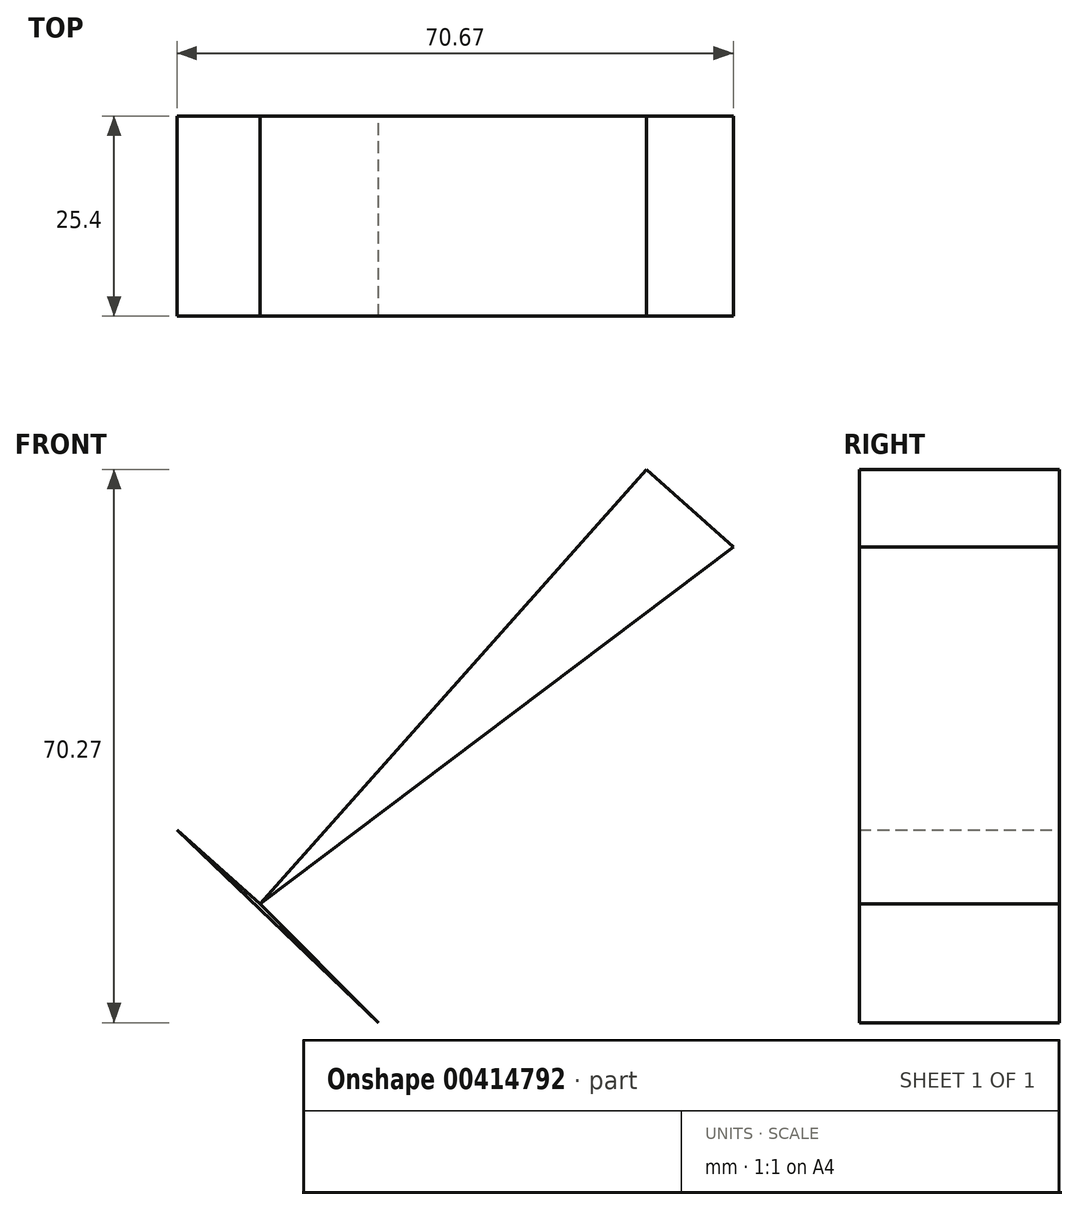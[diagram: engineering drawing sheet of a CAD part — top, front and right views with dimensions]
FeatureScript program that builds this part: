
annotation { "Feature Type Name" : "Feature", "Feature Type Description" : "" }
export const myFeature = defineFeature(function(context is Context, id is Id, definition is map)
    precondition{}
    {
        {
            var Q0;
            Q0=qCreatedBy(makeId("Front.planeOp"),FACE);
            var sketch = newSketch(context, id + "F0", { "sketchPlane" : qUnion([Q0])});
            skLineSegment(sketch, "E0", {"start": v(0, 9.82) * mm, "end": v(0, 0) * mm});
            skLineSegment(sketch, "E1", {"start": v(0, 0) * mm, "end": v(11.04, 0) * mm});
            skLineSegment(sketch, "E2", {"start": v(11.04, 0) * mm, "end": v(0, 9.82) * mm});
            skLineSegment(sketch, "E3", {"start": v(0, 9.82) * mm, "end": v(-49.06, -45.35) * mm});
            skLineSegment(sketch, "E4", {"start": v(-49.06, -45.35) * mm, "end": v(-59.63, -35.95) * mm});
            skLineSegment(sketch, "E5", {"start": v(-59.63, -35.95) * mm, "end": v(-34.01, -60.45) * mm});
            skLineSegment(sketch, "E6", {"start": v(-34.01, -60.45) * mm, "end": v(-49.06, -45.35) * mm});
            skLineSegment(sketch, "E7", {"start": v(11.04, 0) * mm, "end": v(-49.06, -45.35) * mm});
            skSolve(sketch);
        }
        {
            var Q0;
            Q0 = qSketchRegion(id + "F0", true);
            var Q1;
            Q1=makeQuery(id+"F0.imprint","IMPRINT",FACE,{"disambiguationData":[TD([[makeQuery(id+"F0.imprint","IMPRINT",EDGE,{"derivedFrom":sQuery(id+"F0.wireOp",EDGE,"E0")}),-1.0]])]});
            extrude(context, id + "F1", {"entities" : qUnion([Q0, Q1]), "depth" : 25.4 * mm});
        }
    });
